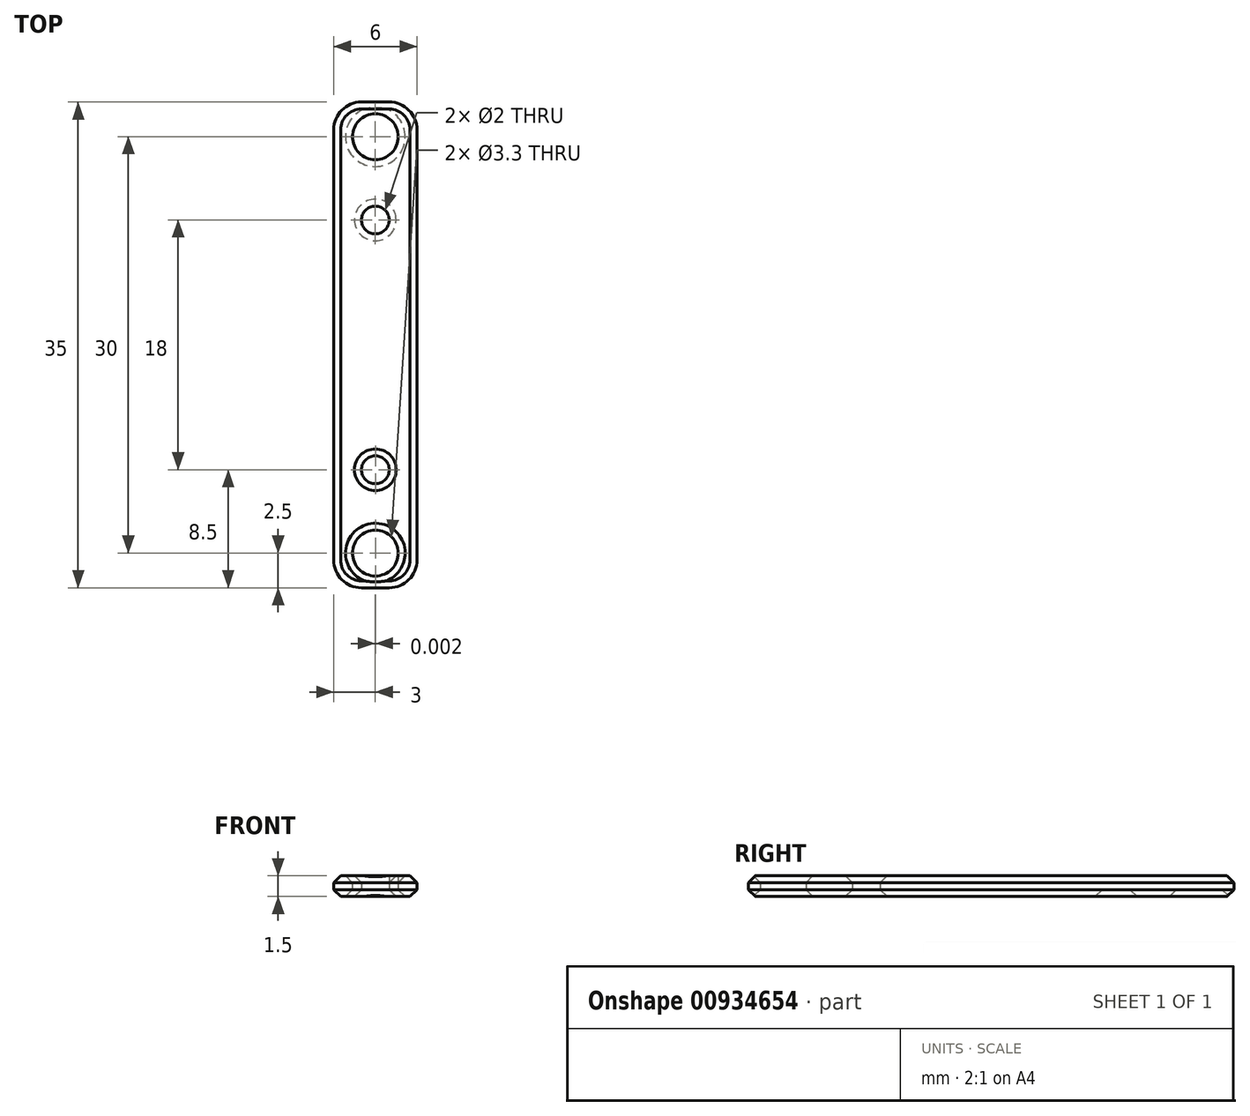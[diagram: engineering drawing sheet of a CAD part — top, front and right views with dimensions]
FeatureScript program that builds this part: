
annotation { "Feature Type Name" : "Feature", "Feature Type Description" : "" }
export const myFeature = defineFeature(function(context is Context, id is Id, definition is map)
    precondition{}
    {
        {
            var Q0;
            Q0=qCreatedBy(makeId("Top.planeOp"),FACE);
            var sketch = newSketch(context, id + "F0", { "sketchPlane" : qUnion([Q0])});
            skLineSegment(sketch, "E0.bottom", {"start": v(-3, 17.5) * mm, "end": v(3, 17.5) * mm});
            skLineSegment(sketch, "E0.top", {"start": v(-3, -17.5) * mm, "end": v(3, -17.5) * mm});
            skLineSegment(sketch, "E0.left", {"start": v(-3, 17.5) * mm, "end": v(-3, -17.5) * mm});
            skLineSegment(sketch, "E0.right", {"start": v(3, 17.5) * mm, "end": v(3, -17.5) * mm});
            skPoint(sketch, "E0.middle", {"position": v(0, 0) * mm});
            skCircle(sketch, "E1", {"center": v(0, 9) * mm, "radius": 1 * mm});
            skCircle(sketch, "E2", {"center": v(0, -9) * mm, "radius": 1 * mm});
            skCircle(sketch, "E3", {"center": v(0, 15) * mm, "radius": 1.65 * mm});
            skCircle(sketch, "E4", {"center": v(0, -15) * mm, "radius": 1.65 * mm});
            skSolve(sketch);
        }
        {
            var Q0;
            Q0=makeQuery(id+"F0.imprint","IMPRINT",FACE,{"disambiguationData":[TD([[makeQuery(id+"F0.imprint","IMPRINT",EDGE,{"derivedFrom":sQuery(id+"F0.wireOp",EDGE,"E0.bottom")}),-1.0]])]});
            extrude(context, id + "F1", {"entities" : qUnion([Q0]), "depth" : 1.5 * mm, "offsetDistance" : 25 * mm});
        }
        {
            var Q0;
            Q0=makeQuery(id+"F1.opExtrude","SWEPT_EDGE",EDGE,{"disambiguationData":[OSD([sQuery(id+"F0.wireOp",EDGE,"E0.bottom"),sQuery(id+"F0.wireOp",EDGE,"E0.left")])]});
            var Q1;
            Q1=makeQuery(id+"F1.opExtrude","SWEPT_EDGE",EDGE,{"disambiguationData":[OSD([sQuery(id+"F0.wireOp",EDGE,"E0.bottom"),sQuery(id+"F0.wireOp",EDGE,"E0.right")])]});
            var Q2;
            Q2=makeQuery(id+"F1.opExtrude","SWEPT_EDGE",EDGE,{"disambiguationData":[OSD([sQuery(id+"F0.wireOp",EDGE,"E0.top"),sQuery(id+"F0.wireOp",EDGE,"E0.left")])]});
            var Q3;
            Q3=makeQuery(id+"F1.opExtrude","SWEPT_EDGE",EDGE,{"disambiguationData":[OSD([sQuery(id+"F0.wireOp",EDGE,"E0.top"),sQuery(id+"F0.wireOp",EDGE,"E0.right")])]});
            fillet(context, id + "F2", {"entities" : qUnion([Q0, Q1, Q2, Q3]), "radius" : 2 * mm, "tangentPropagation" : true, "allowEdgeOverflow" : false});
        }
        {
            var Q0;
            Q0=makeQuery(id+"F1.opExtrude","CAP_EDGE",EDGE,{"disambiguationData":[OSD([sQuery(id+"F0.wireOp",EDGE,"E0.left")])],"isStart":false});
            var Q1;
            Q1=makeQuery(id+"F1.opExtrude","CAP_EDGE",EDGE,{"disambiguationData":[OSD([sQuery(id+"F0.wireOp",EDGE,"E0.right")])],"isStart":false});
            var Q2;
            {var subQ0=sQuery(id+"F0.wireOp",EDGE,"E0.right");var subQ1=sQuery(id+"F0.wireOp",EDGE,"E0.bottom");Q2=makeQuery(id+"F2.opFillet","BLEND_EDGE",EDGE,{"blendedFrom":[makeQuery(id+"F1.opExtrude","SWEPT_EDGE",EDGE,{"disambiguationData":[OSD([subQ1,subQ0])]}),makeQuery(id+"F1.opExtrude","CAP_FACE",FACE,{"disambiguationData":[OSD([subQ1,sQuery(id+"F0.wireOp",EDGE,"E0.top"),sQuery(id+"F0.wireOp",EDGE,"E0.left"),subQ0,sQuery(id+"F0.wireOp",EDGE,"E1"),sQuery(id+"F0.wireOp",EDGE,"E2"),sQuery(id+"F0.wireOp",EDGE,"E3"),sQuery(id+"F0.wireOp",EDGE,"E4")])],"isStart":false})],"blendedInto":[makeQuery(id+"F1.opExtrude","CAP_FACE",FACE,{"disambiguationData":[OSD([subQ1,sQuery(id+"F0.wireOp",EDGE,"E0.top"),sQuery(id+"F0.wireOp",EDGE,"E0.left"),subQ0,sQuery(id+"F0.wireOp",EDGE,"E1"),sQuery(id+"F0.wireOp",EDGE,"E2"),sQuery(id+"F0.wireOp",EDGE,"E3"),sQuery(id+"F0.wireOp",EDGE,"E4")])],"isStart":false})]});}
            var Q3;
            Q3=makeQuery(id+"F1.opExtrude","CAP_EDGE",EDGE,{"disambiguationData":[OSD([sQuery(id+"F0.wireOp",EDGE,"E0.bottom")])],"isStart":false});
            var Q4;
            {var subQ0=sQuery(id+"F0.wireOp",EDGE,"E0.left");var subQ1=sQuery(id+"F0.wireOp",EDGE,"E0.bottom");Q4=makeQuery(id+"F2.opFillet","BLEND_EDGE",EDGE,{"blendedFrom":[makeQuery(id+"F1.opExtrude","SWEPT_EDGE",EDGE,{"disambiguationData":[OSD([subQ1,subQ0])]}),makeQuery(id+"F1.opExtrude","CAP_FACE",FACE,{"disambiguationData":[OSD([subQ1,sQuery(id+"F0.wireOp",EDGE,"E0.top"),subQ0,sQuery(id+"F0.wireOp",EDGE,"E0.right"),sQuery(id+"F0.wireOp",EDGE,"E1"),sQuery(id+"F0.wireOp",EDGE,"E2"),sQuery(id+"F0.wireOp",EDGE,"E3"),sQuery(id+"F0.wireOp",EDGE,"E4")])],"isStart":false})],"blendedInto":[makeQuery(id+"F1.opExtrude","CAP_FACE",FACE,{"disambiguationData":[OSD([subQ1,sQuery(id+"F0.wireOp",EDGE,"E0.top"),subQ0,sQuery(id+"F0.wireOp",EDGE,"E0.right"),sQuery(id+"F0.wireOp",EDGE,"E1"),sQuery(id+"F0.wireOp",EDGE,"E2"),sQuery(id+"F0.wireOp",EDGE,"E3"),sQuery(id+"F0.wireOp",EDGE,"E4")])],"isStart":false})]});}
            var Q5;
            {var subQ0=sQuery(id+"F0.wireOp",EDGE,"E0.left");var subQ1=sQuery(id+"F0.wireOp",EDGE,"E0.top");Q5=makeQuery(id+"F2.opFillet","BLEND_EDGE",EDGE,{"blendedFrom":[makeQuery(id+"F1.opExtrude","SWEPT_EDGE",EDGE,{"disambiguationData":[OSD([subQ1,subQ0])]}),makeQuery(id+"F1.opExtrude","CAP_FACE",FACE,{"disambiguationData":[OSD([sQuery(id+"F0.wireOp",EDGE,"E0.bottom"),subQ1,subQ0,sQuery(id+"F0.wireOp",EDGE,"E0.right"),sQuery(id+"F0.wireOp",EDGE,"E1"),sQuery(id+"F0.wireOp",EDGE,"E2"),sQuery(id+"F0.wireOp",EDGE,"E3"),sQuery(id+"F0.wireOp",EDGE,"E4")])],"isStart":false})],"blendedInto":[makeQuery(id+"F1.opExtrude","CAP_FACE",FACE,{"disambiguationData":[OSD([sQuery(id+"F0.wireOp",EDGE,"E0.bottom"),subQ1,subQ0,sQuery(id+"F0.wireOp",EDGE,"E0.right"),sQuery(id+"F0.wireOp",EDGE,"E1"),sQuery(id+"F0.wireOp",EDGE,"E2"),sQuery(id+"F0.wireOp",EDGE,"E3"),sQuery(id+"F0.wireOp",EDGE,"E4")])],"isStart":false})]});}
            var Q6;
            Q6=makeQuery(id+"F1.opExtrude","CAP_EDGE",EDGE,{"disambiguationData":[OSD([sQuery(id+"F0.wireOp",EDGE,"E0.top")])],"isStart":false});
            var Q7;
            {var subQ0=sQuery(id+"F0.wireOp",EDGE,"E0.right");var subQ1=sQuery(id+"F0.wireOp",EDGE,"E0.top");Q7=makeQuery(id+"F2.opFillet","BLEND_EDGE",EDGE,{"blendedFrom":[makeQuery(id+"F1.opExtrude","SWEPT_EDGE",EDGE,{"disambiguationData":[OSD([subQ1,subQ0])]}),makeQuery(id+"F1.opExtrude","CAP_FACE",FACE,{"disambiguationData":[OSD([sQuery(id+"F0.wireOp",EDGE,"E0.bottom"),subQ1,sQuery(id+"F0.wireOp",EDGE,"E0.left"),subQ0,sQuery(id+"F0.wireOp",EDGE,"E1"),sQuery(id+"F0.wireOp",EDGE,"E2"),sQuery(id+"F0.wireOp",EDGE,"E3"),sQuery(id+"F0.wireOp",EDGE,"E4")])],"isStart":false})],"blendedInto":[makeQuery(id+"F1.opExtrude","CAP_FACE",FACE,{"disambiguationData":[OSD([sQuery(id+"F0.wireOp",EDGE,"E0.bottom"),subQ1,sQuery(id+"F0.wireOp",EDGE,"E0.left"),subQ0,sQuery(id+"F0.wireOp",EDGE,"E1"),sQuery(id+"F0.wireOp",EDGE,"E2"),sQuery(id+"F0.wireOp",EDGE,"E3"),sQuery(id+"F0.wireOp",EDGE,"E4")])],"isStart":false})]});}
            var Q8;
            {var subQ0=sQuery(id+"F0.wireOp",EDGE,"E0.left");var subQ1=sQuery(id+"F0.wireOp",EDGE,"E0.bottom");Q8=makeQuery(id+"F2.opFillet","BLEND_EDGE",EDGE,{"blendedFrom":[makeQuery(id+"F1.opExtrude","SWEPT_EDGE",EDGE,{"disambiguationData":[OSD([subQ1,subQ0])]}),makeQuery(id+"F1.opExtrude","CAP_FACE",FACE,{"disambiguationData":[OSD([subQ1,sQuery(id+"F0.wireOp",EDGE,"E0.top"),subQ0,sQuery(id+"F0.wireOp",EDGE,"E0.right"),sQuery(id+"F0.wireOp",EDGE,"E1"),sQuery(id+"F0.wireOp",EDGE,"E2"),sQuery(id+"F0.wireOp",EDGE,"E3"),sQuery(id+"F0.wireOp",EDGE,"E4")])],"isStart":true})],"blendedInto":[makeQuery(id+"F1.opExtrude","CAP_FACE",FACE,{"disambiguationData":[OSD([subQ1,sQuery(id+"F0.wireOp",EDGE,"E0.top"),subQ0,sQuery(id+"F0.wireOp",EDGE,"E0.right"),sQuery(id+"F0.wireOp",EDGE,"E1"),sQuery(id+"F0.wireOp",EDGE,"E2"),sQuery(id+"F0.wireOp",EDGE,"E3"),sQuery(id+"F0.wireOp",EDGE,"E4")])],"isStart":true})]});}
            var Q9;
            Q9=makeQuery(id+"F1.opExtrude","CAP_EDGE",EDGE,{"disambiguationData":[OSD([sQuery(id+"F0.wireOp",EDGE,"E0.bottom")])],"isStart":true});
            var Q10;
            {var subQ0=sQuery(id+"F0.wireOp",EDGE,"E0.right");var subQ1=sQuery(id+"F0.wireOp",EDGE,"E0.bottom");Q10=makeQuery(id+"F2.opFillet","BLEND_EDGE",EDGE,{"blendedFrom":[makeQuery(id+"F1.opExtrude","SWEPT_EDGE",EDGE,{"disambiguationData":[OSD([subQ1,subQ0])]}),makeQuery(id+"F1.opExtrude","CAP_FACE",FACE,{"disambiguationData":[OSD([subQ1,sQuery(id+"F0.wireOp",EDGE,"E0.top"),sQuery(id+"F0.wireOp",EDGE,"E0.left"),subQ0,sQuery(id+"F0.wireOp",EDGE,"E1"),sQuery(id+"F0.wireOp",EDGE,"E2"),sQuery(id+"F0.wireOp",EDGE,"E3"),sQuery(id+"F0.wireOp",EDGE,"E4")])],"isStart":true})],"blendedInto":[makeQuery(id+"F1.opExtrude","CAP_FACE",FACE,{"disambiguationData":[OSD([subQ1,sQuery(id+"F0.wireOp",EDGE,"E0.top"),sQuery(id+"F0.wireOp",EDGE,"E0.left"),subQ0,sQuery(id+"F0.wireOp",EDGE,"E1"),sQuery(id+"F0.wireOp",EDGE,"E2"),sQuery(id+"F0.wireOp",EDGE,"E3"),sQuery(id+"F0.wireOp",EDGE,"E4")])],"isStart":true})]});}
            var Q11;
            Q11=makeQuery(id+"F1.opExtrude","CAP_EDGE",EDGE,{"disambiguationData":[OSD([sQuery(id+"F0.wireOp",EDGE,"E0.right")])],"isStart":true});
            var Q12;
            Q12=makeQuery(id+"F1.opExtrude","CAP_EDGE",EDGE,{"disambiguationData":[OSD([sQuery(id+"F0.wireOp",EDGE,"E0.left")])],"isStart":true});
            var Q13;
            {var subQ0=sQuery(id+"F0.wireOp",EDGE,"E0.left");var subQ1=sQuery(id+"F0.wireOp",EDGE,"E0.top");Q13=makeQuery(id+"F2.opFillet","BLEND_EDGE",EDGE,{"blendedFrom":[makeQuery(id+"F1.opExtrude","SWEPT_EDGE",EDGE,{"disambiguationData":[OSD([subQ1,subQ0])]}),makeQuery(id+"F1.opExtrude","CAP_FACE",FACE,{"disambiguationData":[OSD([sQuery(id+"F0.wireOp",EDGE,"E0.bottom"),subQ1,subQ0,sQuery(id+"F0.wireOp",EDGE,"E0.right"),sQuery(id+"F0.wireOp",EDGE,"E1"),sQuery(id+"F0.wireOp",EDGE,"E2"),sQuery(id+"F0.wireOp",EDGE,"E3"),sQuery(id+"F0.wireOp",EDGE,"E4")])],"isStart":true})],"blendedInto":[makeQuery(id+"F1.opExtrude","CAP_FACE",FACE,{"disambiguationData":[OSD([sQuery(id+"F0.wireOp",EDGE,"E0.bottom"),subQ1,subQ0,sQuery(id+"F0.wireOp",EDGE,"E0.right"),sQuery(id+"F0.wireOp",EDGE,"E1"),sQuery(id+"F0.wireOp",EDGE,"E2"),sQuery(id+"F0.wireOp",EDGE,"E3"),sQuery(id+"F0.wireOp",EDGE,"E4")])],"isStart":true})]});}
            var Q14;
            Q14=makeQuery(id+"F1.opExtrude","CAP_EDGE",EDGE,{"disambiguationData":[OSD([sQuery(id+"F0.wireOp",EDGE,"E0.top")])],"isStart":true});
            var Q15;
            {var subQ0=sQuery(id+"F0.wireOp",EDGE,"E0.right");var subQ1=sQuery(id+"F0.wireOp",EDGE,"E0.top");Q15=makeQuery(id+"F2.opFillet","BLEND_EDGE",EDGE,{"blendedFrom":[makeQuery(id+"F1.opExtrude","SWEPT_EDGE",EDGE,{"disambiguationData":[OSD([subQ1,subQ0])]}),makeQuery(id+"F1.opExtrude","CAP_FACE",FACE,{"disambiguationData":[OSD([sQuery(id+"F0.wireOp",EDGE,"E0.bottom"),subQ1,sQuery(id+"F0.wireOp",EDGE,"E0.left"),subQ0,sQuery(id+"F0.wireOp",EDGE,"E1"),sQuery(id+"F0.wireOp",EDGE,"E2"),sQuery(id+"F0.wireOp",EDGE,"E3"),sQuery(id+"F0.wireOp",EDGE,"E4")])],"isStart":true})],"blendedInto":[makeQuery(id+"F1.opExtrude","CAP_FACE",FACE,{"disambiguationData":[OSD([sQuery(id+"F0.wireOp",EDGE,"E0.bottom"),subQ1,sQuery(id+"F0.wireOp",EDGE,"E0.left"),subQ0,sQuery(id+"F0.wireOp",EDGE,"E1"),sQuery(id+"F0.wireOp",EDGE,"E2"),sQuery(id+"F0.wireOp",EDGE,"E3"),sQuery(id+"F0.wireOp",EDGE,"E4")])],"isStart":true})]});}
            var Q16;
            Q16=makeQuery(id+"F1.opExtrude","CAP_EDGE",EDGE,{"disambiguationData":[OSD([sQuery(id+"F0.wireOp",EDGE,"E2")])],"isStart":true});
            var Q17;
            Q17=makeQuery(id+"F1.opExtrude","CAP_EDGE",EDGE,{"disambiguationData":[OSD([sQuery(id+"F0.wireOp",EDGE,"E1")])],"isStart":true});
            var Q18;
            Q18=makeQuery(id+"F1.opExtrude","CAP_EDGE",EDGE,{"disambiguationData":[OSD([sQuery(id+"F0.wireOp",EDGE,"E3")])],"isStart":true});
            var Q19;
            Q19=makeQuery(id+"F1.opExtrude","CAP_EDGE",EDGE,{"disambiguationData":[OSD([sQuery(id+"F0.wireOp",EDGE,"E2")])],"isStart":false});
            var Q20;
            Q20=makeQuery(id+"F1.opExtrude","CAP_EDGE",EDGE,{"disambiguationData":[OSD([sQuery(id+"F0.wireOp",EDGE,"E4")])],"isStart":false});
            var Q21;
            Q21=makeQuery(id+"F1.opExtrude","CAP_EDGE",EDGE,{"disambiguationData":[OSD([sQuery(id+"F0.wireOp",EDGE,"E4")])],"isStart":true});
            chamfer(context, id + "F3", {"entities" : qUnion([Q0, Q1, Q2, Q3, Q4, Q5, Q6, Q7, Q8, Q9, Q10, Q11, Q12, Q13, Q14, Q15, Q16, Q17, Q18, Q19, Q20, Q21]), "width" : 0.5 * mm, "tangentPropagation" : true});
        }
    });
